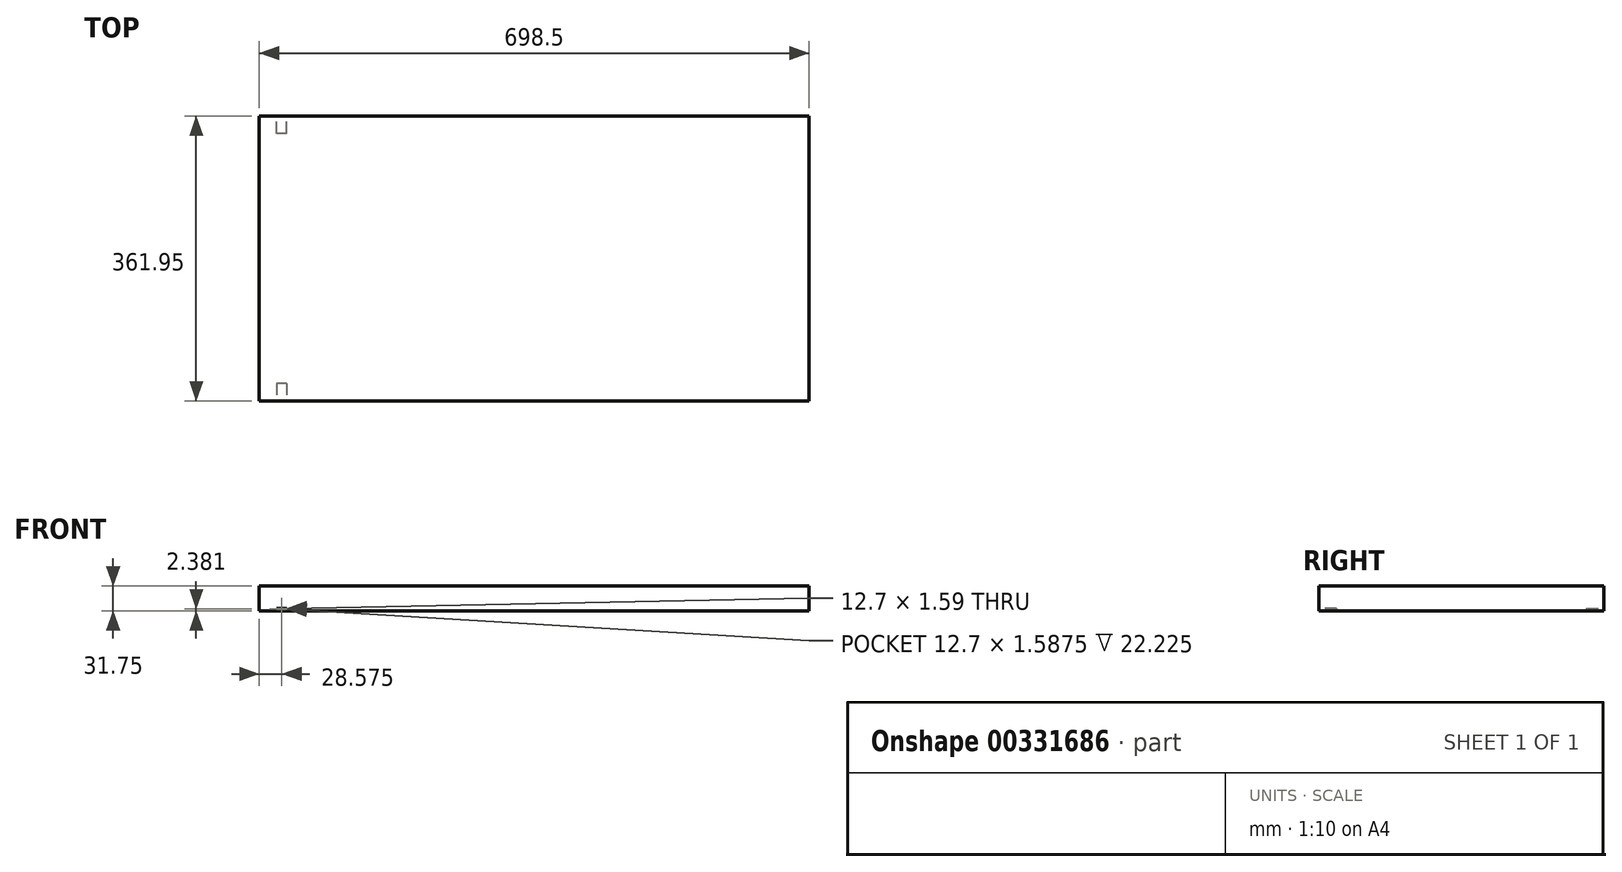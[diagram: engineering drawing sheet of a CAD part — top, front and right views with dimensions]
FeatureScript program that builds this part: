
annotation { "Feature Type Name" : "Feature", "Feature Type Description" : "" }
export const myFeature = defineFeature(function(context is Context, id is Id, definition is map)
    precondition{}
    {
        {
            var Q0;
            Q0=qCreatedBy(makeId("Front.planeOp"),FACE);
            var sketch = newSketch(context, id + "F0", { "sketchPlane" : qUnion([Q0])});
            skLineSegment(sketch, "E0", {"start": v(-149.75, 0) * mm, "end": v(548.75, 0) * mm});
            skLineSegment(sketch, "E1", {"start": v(548.75, 0) * mm, "end": v(548.75, -31.75) * mm});
            skLineSegment(sketch, "E2", {"start": v(548.75, -31.75) * mm, "end": v(-149.75, -31.75) * mm});
            skLineSegment(sketch, "E3", {"start": v(-149.75, -31.75) * mm, "end": v(-149.75, 0) * mm});
            skSolve(sketch);
        }
        {
            var Q0;
            Q0=makeQuery(id+"F0.imprint","IMPRINT",FACE,{"disambiguationData":[TD([[makeQuery(id+"F0.imprint","IMPRINT",EDGE,{"derivedFrom":sQuery(id+"F0.wireOp",EDGE,"E0")}),-1.0]])]});
            extrude(context, id + "F1", {"entities" : qUnion([Q0]), "oppositeDirection" : true, "depth" : 361.95 * mm});
        }
        {
            var Q0;
            Q0=makeQuery(id+"F0.imprint","IMPRINT",FACE,{"disambiguationData":[TD([[makeQuery(id+"F0.imprint","IMPRINT",EDGE,{"derivedFrom":sQuery(id+"F0.wireOp",EDGE,"E0")}),-1.0]])]});
            var sketch = newSketch(context, id + "F2", { "sketchPlane" : qUnion([Q0])});
            skLineSegment(sketch, "E4.bottom", {"start": v(-114.82, -28.58) * mm, "end": v(-127.52, -28.58) * mm});
            skLineSegment(sketch, "E4.top", {"start": v(-114.82, -30.16) * mm, "end": v(-127.52, -30.16) * mm});
            skLineSegment(sketch, "E4.left", {"start": v(-114.82, -28.58) * mm, "end": v(-114.82, -30.16) * mm});
            skLineSegment(sketch, "E4.right", {"start": v(-127.52, -28.58) * mm, "end": v(-127.52, -30.16) * mm});
            skSolve(sketch);
        }
        {
            var Q0;
            Q0 = qSketchRegion(id + "F2", true);
            extrude(context, id + "F3", {"entities" : qUnion([Q0]), "operationType" : NewBodyOperationType.REMOVE, "oppositeDirection" : true, "depth" : 22.22 * mm});
        }
        {
            var Q0;
            Q0=makeQuery(id+"F1.opExtrude","CAP_FACE",FACE,{"disambiguationData":[OSD([sQuery(id+"F0.wireOp",EDGE,"E0"),sQuery(id+"F0.wireOp",EDGE,"E1"),sQuery(id+"F0.wireOp",EDGE,"E2"),sQuery(id+"F0.wireOp",EDGE,"E3")])],"isStart":false});
            var sketch = newSketch(context, id + "F4", { "sketchPlane" : qUnion([Q0])});
            skLineSegment(sketch, "E5.bottom", {"start": v(114.82, -28.58) * mm, "end": v(127.52, -28.58) * mm});
            skLineSegment(sketch, "E5.top", {"start": v(114.82, -30.16) * mm, "end": v(127.52, -30.16) * mm});
            skLineSegment(sketch, "E5.left", {"start": v(114.82, -28.58) * mm, "end": v(114.82, -30.16) * mm});
            skLineSegment(sketch, "E5.right", {"start": v(127.52, -28.58) * mm, "end": v(127.52, -30.16) * mm});
            skSolve(sketch);
        }
        {
            var Q0;
            Q0 = qSketchRegion(id + "F4", true);
            extrude(context, id + "F5", {"entities" : qUnion([Q0]), "operationType" : NewBodyOperationType.REMOVE, "oppositeDirection" : true, "depth" : 22.22 * mm});
        }
    });
